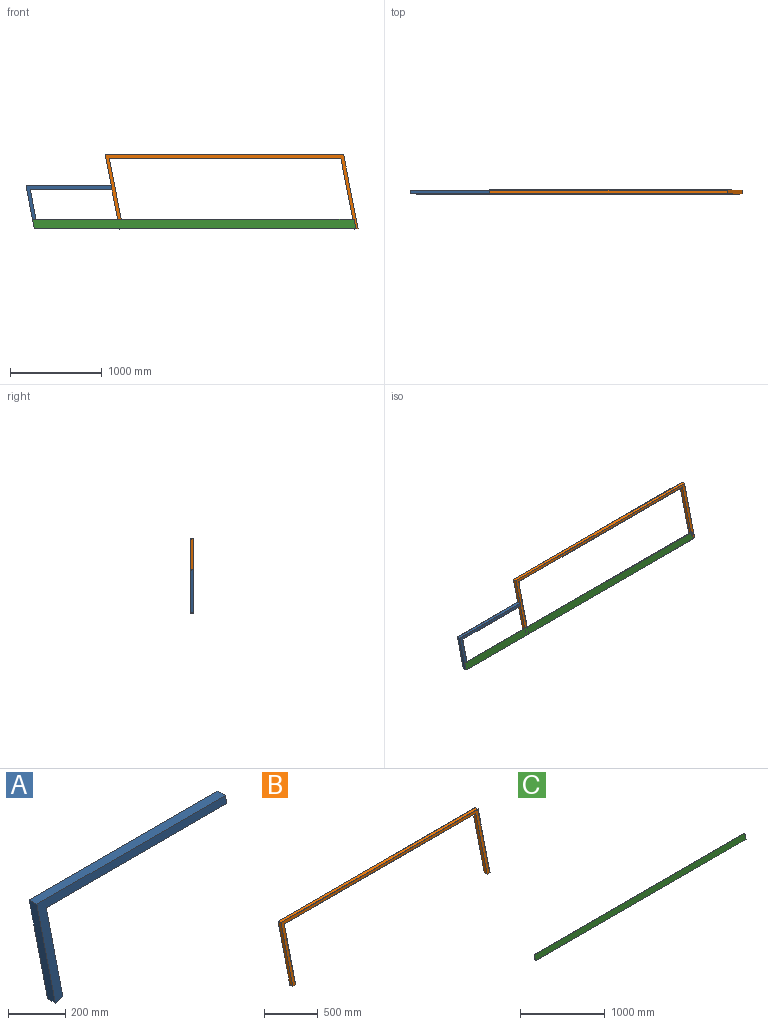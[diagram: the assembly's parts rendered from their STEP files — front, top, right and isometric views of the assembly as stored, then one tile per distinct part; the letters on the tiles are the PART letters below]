
ASSEMBLY  parts=3 mates=2
PART A: 14 faces, bbox 937.5x38.1x467.2 mm
  f0: plane 937.51x467.19mm, normal (0,-1,0), area 51950mm2, adj f7,f8,f9,f10,f11,f13
  f1: plane 896.14x31.75mm, normal (0,0,1), area 28452.5mm2, adj f3,f4,f6,f13
  f2: plane 925.25x31.75mm, normal (0,0,-1), area 29376.8mm2, adj f3,f4,f5,f13
  f3: plane 930.81x461.51mm, normal (0,-1,0), area 38962.5mm2, adj f1,f2,f5,f6,f7,f13
  f4: plane 930.81x461.51mm, normal (0,1,0), area 38962.5mm2, adj f1,f2,f5,f6,f7,f13
  f5: plane 461.51x89.71mm, normal (0.98,0,0.19), area 14927.3mm2, adj f2,f3,f4,f7
  f6: plane 427.49x83.1mm, normal (-0.98,0,-0.19), area 13826.7mm2, adj f1,f3,f4,f7
  f7: plane 38.1x37.4mm, normal (0.19,0,-0.98), area 544.4mm2, adj f0,f3,f4,f5,f6,f10,f11,f12
  f8: plane 930.1x38.1mm, normal (0,0,1), area 35436.9mm2, adj f0,f11,f12,f13
  f9: plane 891.29x38.1mm, normal (0,0,-1), area 33958.2mm2, adj f0,f10,f12,f13
  f10: plane 421.82x81.99mm, normal (0.98,0,0.19), area 16372mm2, adj f0,f7,f9,f12
  f11: plane 467.19x90.81mm, normal (-0.98,0,-0.19), area 18132.9mm2, adj f0,f7,f8,f12
  f12: plane 937.51x467.19mm, normal (0,1,0), area 51950mm2, adj f7,f8,f9,f10,f11,f13
  f13: plane 38.1x38.1mm, normal (0.98,0,0.19), area 554.5mm2, adj f0,f1,f2,f3,f4,f8,f9,f12
PART B: 18 faces, bbox 2761.3x38.1x810.1 mm
  f0: plane 774.55x150.56mm, normal (0.98,0,0.19), area 25052.4mm2, adj f3,f4,f6,f8
  f1: plane 800.25x155.55mm, normal (-0.98,0,-0.19), area 25883.4mm2, adj f2,f4,f6,f8
  f2: plane 2598.73x31.75mm, normal (0,0,-1), area 82509.8mm2, adj f1,f4,f5,f6
  f3: plane 2534.04x31.75mm, normal (0,0,1), area 80455.9mm2, adj f0,f4,f6,f7
  f4: plane 2754.28x806.3mm, normal (0,-1,0), area 132418.6mm2, adj f0,f1,f2,f3,f5,f7,f8,f9
  f5: plane 806.3x156.73mm, normal (0.98,0,0.19), area 26079.3mm2, adj f2,f4,f6,f9
  f6: plane 2754.28x806.3mm, normal (0,1,0), area 132418.6mm2, adj f0,f1,f2,f3,f5,f7,f8,f9
  f7: plane 768.5x149.38mm, normal (-0.98,0,-0.19), area 24856.4mm2, adj f3,f4,f6,f9
  f8: plane 38.1x37.4mm, normal (0.19,0,-0.98), area 443.5mm2, adj f0,f1,f4,f6,f10,f11,f15,f17
  f9: plane 38.1x37.4mm, normal (0.19,0,-0.98), area 443.5mm2, adj f4,f5,f6,f7,f14,f15,f16,f17
  f10: plane 802.82x156.05mm, normal (0.98,0,0.19), area 31159.7mm2, adj f8,f13,f15,f17
  f11: plane 771.99x150.06mm, normal (-0.98,0,-0.19), area 29963.1mm2, adj f8,f12,f15,f17
  f12: plane 2527.58x38.1mm, normal (0,0,-1), area 96300.6mm2, adj f11,f14,f15,f17
  f13: plane 2605.2x38.1mm, normal (0,0,1), area 99258.2mm2, adj f10,f15,f16,f17
  f14: plane 764.72x148.65mm, normal (0.98,0,0.19), area 29681mm2, adj f9,f12,f15,f17
  f15: plane 2761.25x810.09mm, normal (0,-1,0), area 158902.3mm2, adj f8,f9,f10,f11,f12,f13,f14,f16
  f16: plane 810.09x157.46mm, normal (-0.98,0,-0.19), area 31441.9mm2, adj f9,f13,f15,f17
  f17: plane 2761.25x810.09mm, normal (0,1,0), area 158902.3mm2, adj f8,f9,f10,f11,f12,f13,f14,f16
PART C: 6 faces, bbox 3530.6x5x100 mm
  f0: plane 3530.6x100mm, normal (0,-1,0), area 351116.2mm2, adj f2,f3,f4,f5
  f1: plane 3530.6x100mm, normal (0,1,0), area 351116.2mm2, adj f2,f3,f4,f5
  f2: plane 3511.16x5mm, normal (0,0,-1), area 17555.8mm2, adj f0,f1,f4,f5
  f3: plane 3511.16x5mm, normal (0,0,1), area 17555.8mm2, adj f0,f1,f4,f5
  f4: plane 100x19.44mm, normal (0.98,0,0.19), area 509.4mm2, adj f0,f1,f2,f3
  f5: plane 100x19.44mm, normal (-0.98,0,-0.19), area 509.4mm2, adj f0,f1,f2,f3
PLACE A t=(-441.78,-51.5,-89.67)mm
PLACE B t=(1233.69,-51.5,-164.44)mm
PLACE C t=(2222.68,-73.05,-487.8)mm
MATE fastened B.f16 <-> A.f13  axis (-0.98,0,-0.19) through (-357.1,-51.5,-544.35)mm
MATE fastened A.f0 <-> C.f1  axis (0,-1,0) through (-1288.48,-70.55,-537.8)mm
